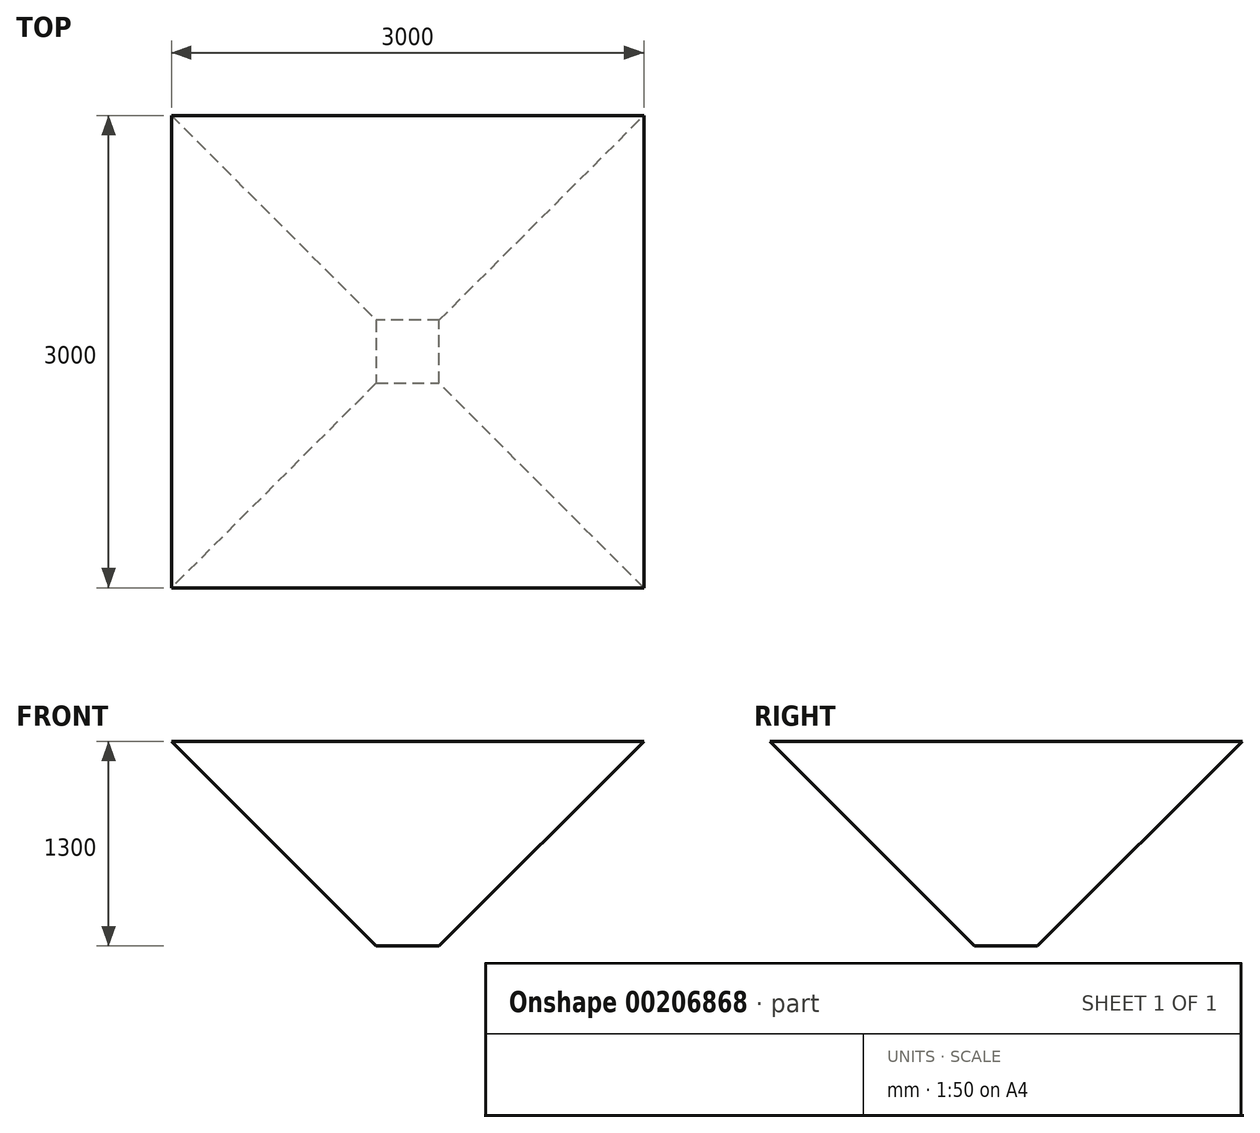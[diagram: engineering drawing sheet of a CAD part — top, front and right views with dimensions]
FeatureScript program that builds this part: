
annotation { "Feature Type Name" : "Feature", "Feature Type Description" : "" }
export const myFeature = defineFeature(function(context is Context, id is Id, definition is map)
    precondition{}
    {
        {
            var Q0;
            Q0=qCreatedBy(makeId("Top.planeOp"),FACE);
            var sketch = newSketch(context, id + "F0", { "sketchPlane" : qUnion([Q0])});
            skLineSegment(sketch, "E0.bottom", {"start": v(1500, -1500) * mm, "end": v(-1500, -1500) * mm});
            skLineSegment(sketch, "E0.top", {"start": v(1500, 1500) * mm, "end": v(-1500, 1500) * mm});
            skLineSegment(sketch, "E0.left", {"start": v(1500, -1500) * mm, "end": v(1500, 1500) * mm});
            skLineSegment(sketch, "E0.right", {"start": v(-1500, -1500) * mm, "end": v(-1500, 1500) * mm});
            skPoint(sketch, "E0.middle", {"position": v(0, 0) * mm});
            skSolve(sketch);
        }
        {
            var Q0;
            Q0 = qSketchRegion(id + "F0", true);
            extrude(context, id + "F1", {"entities" : qUnion([Q0]), "oppositeDirection" : true, "depth" : 1300 * mm, "hasDraft" : true, "draftAngle" : 45 * degree, "draftPullDirection" : true});
        }
    });
